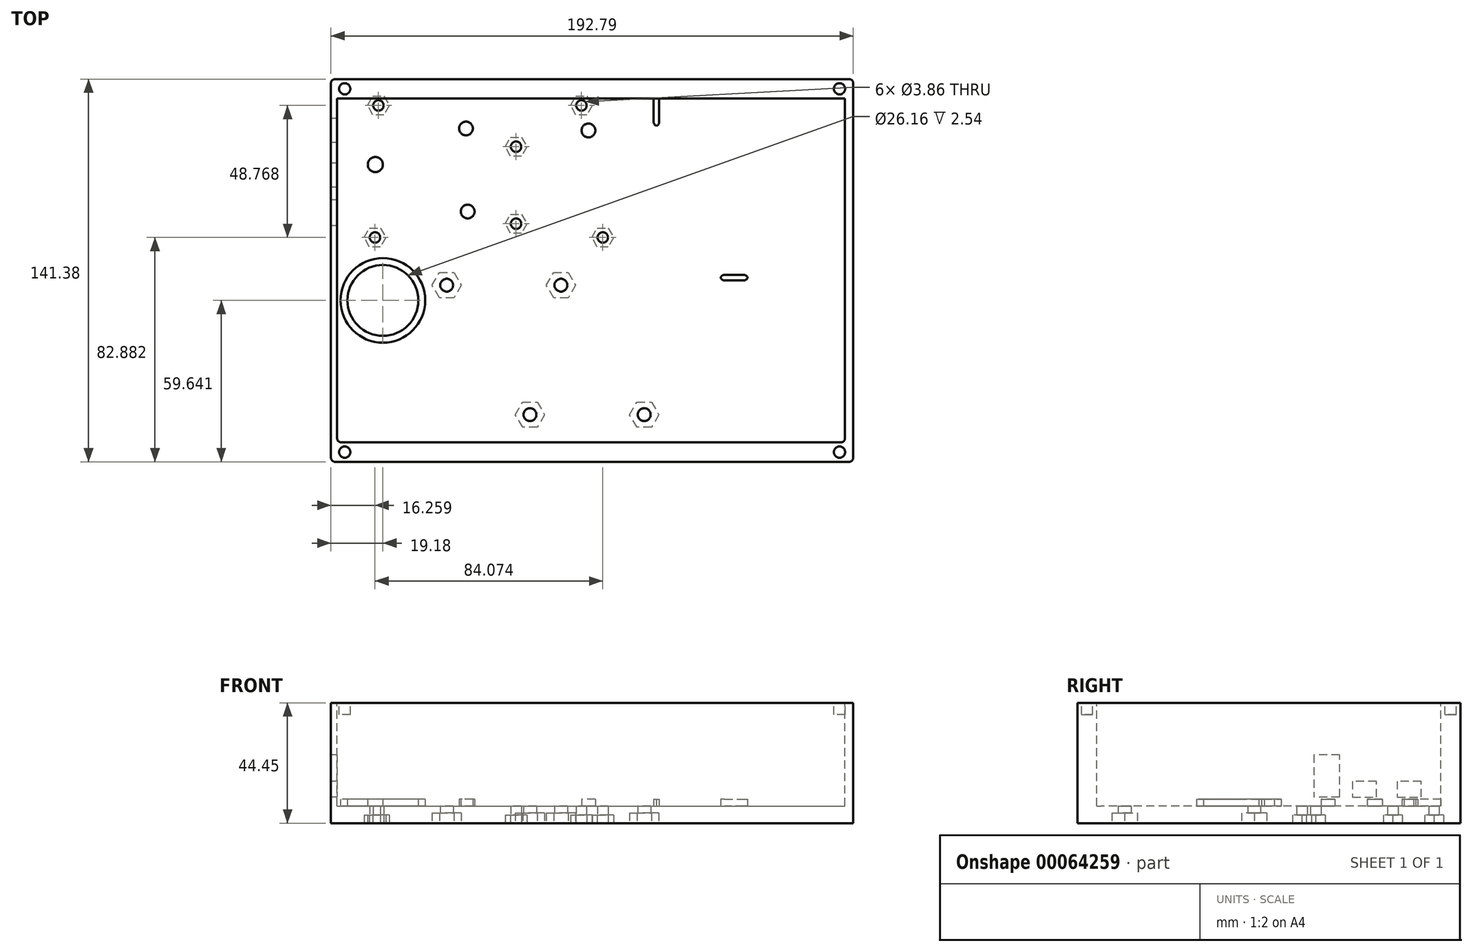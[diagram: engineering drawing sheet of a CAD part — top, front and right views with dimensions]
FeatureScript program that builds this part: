
annotation { "Feature Type Name" : "Feature", "Feature Type Description" : "" }
export const myFeature = defineFeature(function(context is Context, id is Id, definition is map)
    precondition{}
    {
        {
            var Q0;
            Q0=qCreatedBy(makeId("Top.planeOp"),FACE);
            var sketch = newSketch(context, id + "F0", { "sketchPlane" : qUnion([Q0])});
            skLineSegment(sketch, "E0.bottom", {"start": v(-98.88, 40.37) * mm, "end": v(3.23, 40.37) * mm});
            skLineSegment(sketch, "E0.top", {"start": v(-98.88, -13.48) * mm, "end": v(3.23, -13.48) * mm});
            skLineSegment(sketch, "E0.left", {"start": v(-98.88, 40.37) * mm, "end": v(-98.88, -13.48) * mm});
            skLineSegment(sketch, "E0.right", {"start": v(3.23, 40.37) * mm, "end": v(3.23, -13.48) * mm});
            skSolve(sketch);
        }
        {
            var Q0;
            Q0=qCreatedBy(makeId("Top.planeOp"),FACE);
            var sketch = newSketch(context, id + "F1", { "sketchPlane" : qUnion([Q0])});
            skLineSegment(sketch, "E1.bottom", {"start": v(-98.88, 40.37) * mm, "end": v(88.57, 40.37) * mm});
            skLineSegment(sketch, "E1.top", {"start": v(-98.88, -86.63) * mm, "end": v(88.57, -86.63) * mm});
            skLineSegment(sketch, "E1.left", {"start": v(-98.88, 40.37) * mm, "end": v(-98.88, -86.63) * mm});
            skLineSegment(sketch, "E1.right", {"start": v(88.57, 40.37) * mm, "end": v(88.57, -86.63) * mm});
            skSolve(sketch);
        }
        {
            var Q0;
            Q0=qCreatedBy(makeId("Top.planeOp"),FACE);
            var sketch = newSketch(context, id + "F2", { "sketchPlane" : qUnion([Q0])});
            skLineSegment(sketch, "E2", {"start": v(5.77, 40.37) * mm, "end": v(5.77, 30.21) * mm});
            skLineSegment(sketch, "E3", {"start": v(5.77, 30.21) * mm, "end": v(3.23, 30.21) * mm});
            skLineSegment(sketch, "E4", {"start": v(3.23, 30.21) * mm, "end": v(3.23, 40.37) * mm});
            skLineSegment(sketch, "E5", {"start": v(3.23, -3.32) * mm, "end": v(5.77, -3.32) * mm});
            skLineSegment(sketch, "E6", {"start": v(5.77, -3.32) * mm, "end": v(5.77, -16.02) * mm});
            skLineSegment(sketch, "E7", {"start": v(5.77, -16.02) * mm, "end": v(-6.93, -16.02) * mm});
            skLineSegment(sketch, "E8", {"start": v(-6.93, -16.02) * mm, "end": v(-6.93, -13.48) * mm});
            skLineSegment(sketch, "E9", {"start": v(-6.93, -13.48) * mm, "end": v(3.23, -13.48) * mm});
            skLineSegment(sketch, "E10", {"start": v(3.23, -13.48) * mm, "end": v(3.23, -3.32) * mm});
            skLineSegment(sketch, "E11", {"start": v(-6.93, -16.02) * mm, "end": v(-98.88, -16.02) * mm, "construction": true});
            skLineSegment(sketch, "E12", {"start": v(3.23, 40.37) * mm, "end": v(5.77, 40.37) * mm});
            skSolve(sketch);
        }
        {
            var Q0;
            Q0=qCreatedBy(makeId("Top.planeOp"),FACE);
            var sketch = newSketch(context, id + "F3", { "sketchPlane" : qUnion([Q0])});
            skCircle(sketch, "E13", {"center": v(-84.91, -10.94) * mm, "radius": 1.93 * mm});
            skCircle(sketch, "E14", {"center": v(-32.84, -5.86) * mm, "radius": 1.93 * mm});
            skCircle(sketch, "E15", {"center": v(-32.84, 22.6) * mm, "radius": 1.93 * mm});
            skCircle(sketch, "E16", {"center": v(-8.71, 37.83) * mm, "radius": 1.93 * mm});
            skCircle(sketch, "E17", {"center": v(-83.64, 37.83) * mm, "radius": 1.93 * mm});
            skCircle(sketch, "E18", {"center": v(-0.84, -10.94) * mm, "radius": 1.93 * mm});
            skLineSegment(sketch, "E19", {"start": v(-32.84, 40.38) * mm, "end": v(-32.84, -13.48) * mm, "construction": true});
            skLineSegment(sketch, "E20", {"start": v(-32.84, 22.6) * mm, "end": v(3.23, 22.6) * mm, "construction": true});
            skSolve(sketch);
        }
        {
            var Q0;
            Q0=qCreatedBy(makeId("Top.planeOp"),FACE);
            var sketch = newSketch(context, id + "F4", { "sketchPlane" : qUnion([Q0])});
            skCircle(sketch, "E21", {"center": v(-81.99, -34.18) * mm, "radius": 13.08 * mm});
            skCircle(sketch, "E22", {"center": v(-81.99, -34.18) * mm, "radius": 15.62 * mm});
            skSolve(sketch);
        }
        {
            var Q0;
            Q0=qCreatedBy(makeId("Top.planeOp"),FACE);
            var sketch = newSketch(context, id + "F5", { "sketchPlane" : qUnion([Q0])});
            skLineSegment(sketch, "E23.bottom", {"start": v(-101.17, 47.56) * mm, "end": v(91.62, 47.56) * mm});
            skLineSegment(sketch, "E23.top", {"start": v(-101.17, -93.82) * mm, "end": v(91.62, -93.82) * mm});
            skLineSegment(sketch, "E23.left", {"start": v(-101.17, 47.56) * mm, "end": v(-101.17, -93.82) * mm});
            skLineSegment(sketch, "E23.right", {"start": v(91.62, 47.56) * mm, "end": v(91.62, -93.82) * mm});
            skSolve(sketch);
        }
        {
            var Q0;
            Q0=makeQuery(id+"F5.imprint","IMPRINT",FACE,{"disambiguationData":[TD([[makeQuery(id+"F5.imprint","IMPRINT",EDGE,{"derivedFrom":sQuery(id+"F5.wireOp",EDGE,"E23.bottom")}),-1.0]])]});
            var sketch = newSketch(context, id + "F6", { "sketchPlane" : qUnion([Q0])});
            skCircle(sketch, "E24.cCircle", {"center": v(-83.64, 37.83) * mm, "radius": 3.5 * mm, "construction": true});
            skLineSegment(sketch, "E24.0", {"start": v(-79.6, 37.83) * mm, "end": v(-81.62, 34.34) * mm});
            skLineSegment(sketch, "E24.1", {"start": v(-81.62, 34.34) * mm, "end": v(-85.66, 34.34) * mm});
            skLineSegment(sketch, "E24.2", {"start": v(-85.66, 34.34) * mm, "end": v(-87.67, 37.83) * mm});
            skLineSegment(sketch, "E24.3", {"start": v(-87.67, 37.83) * mm, "end": v(-85.66, 41.32) * mm});
            skLineSegment(sketch, "E24.4", {"start": v(-85.66, 41.32) * mm, "end": v(-81.62, 41.32) * mm});
            skLineSegment(sketch, "E24.5", {"start": v(-81.62, 41.32) * mm, "end": v(-79.6, 37.83) * mm});
            skPoint(sketch, "E24.0.midPoint", {"position": v(-80.62, 36.08) * mm});
            skCircle(sketch, "E25.cCircle", {"center": v(-8.71, 37.83) * mm, "radius": 3.5 * mm, "construction": true});
            skLineSegment(sketch, "E25.0", {"start": v(-4.68, 37.83) * mm, "end": v(-6.7, 34.34) * mm});
            skLineSegment(sketch, "E25.1", {"start": v(-6.7, 34.34) * mm, "end": v(-10.73, 34.34) * mm});
            skLineSegment(sketch, "E25.2", {"start": v(-10.73, 34.34) * mm, "end": v(-12.74, 37.83) * mm});
            skLineSegment(sketch, "E25.3", {"start": v(-12.74, 37.83) * mm, "end": v(-10.73, 41.32) * mm});
            skLineSegment(sketch, "E25.4", {"start": v(-10.73, 41.32) * mm, "end": v(-6.7, 41.32) * mm});
            skLineSegment(sketch, "E25.5", {"start": v(-6.7, 41.32) * mm, "end": v(-4.68, 37.83) * mm});
            skPoint(sketch, "E25.0.midPoint", {"position": v(-5.69, 36.08) * mm});
            skCircle(sketch, "E26.cCircle", {"center": v(-32.84, 22.6) * mm, "radius": 3.5 * mm, "construction": true});
            skLineSegment(sketch, "E26.0", {"start": v(-28.8, 22.6) * mm, "end": v(-30.82, 19.1) * mm});
            skLineSegment(sketch, "E26.1", {"start": v(-30.82, 19.1) * mm, "end": v(-34.86, 19.1) * mm});
            skLineSegment(sketch, "E26.2", {"start": v(-34.86, 19.1) * mm, "end": v(-36.87, 22.6) * mm});
            skLineSegment(sketch, "E26.3", {"start": v(-36.87, 22.6) * mm, "end": v(-34.86, 26.08) * mm});
            skLineSegment(sketch, "E26.4", {"start": v(-34.86, 26.08) * mm, "end": v(-30.82, 26.08) * mm});
            skLineSegment(sketch, "E26.5", {"start": v(-30.82, 26.08) * mm, "end": v(-28.8, 22.6) * mm});
            skPoint(sketch, "E26.0.midPoint", {"position": v(-29.82, 20.84) * mm});
            skCircle(sketch, "E27.cCircle", {"center": v(-84.91, -10.94) * mm, "radius": 3.5 * mm, "construction": true});
            skLineSegment(sketch, "E27.0", {"start": v(-80.88, -10.94) * mm, "end": v(-82.9, -14.43) * mm});
            skLineSegment(sketch, "E27.1", {"start": v(-82.9, -14.43) * mm, "end": v(-86.93, -14.43) * mm});
            skLineSegment(sketch, "E27.2", {"start": v(-86.93, -14.43) * mm, "end": v(-88.94, -10.94) * mm});
            skLineSegment(sketch, "E27.3", {"start": v(-88.94, -10.94) * mm, "end": v(-86.93, -7.45) * mm});
            skLineSegment(sketch, "E27.4", {"start": v(-86.93, -7.45) * mm, "end": v(-82.9, -7.45) * mm});
            skLineSegment(sketch, "E27.5", {"start": v(-82.9, -7.45) * mm, "end": v(-80.88, -10.94) * mm});
            skPoint(sketch, "E27.0.midPoint", {"position": v(-81.89, -12.68) * mm});
            skCircle(sketch, "E28.cCircle", {"center": v(-32.84, -5.86) * mm, "radius": 3.5 * mm, "construction": true});
            skLineSegment(sketch, "E28.0", {"start": v(-28.8, -5.86) * mm, "end": v(-30.82, -9.35) * mm});
            skLineSegment(sketch, "E28.1", {"start": v(-30.82, -9.35) * mm, "end": v(-34.86, -9.35) * mm});
            skLineSegment(sketch, "E28.2", {"start": v(-34.86, -9.35) * mm, "end": v(-36.87, -5.86) * mm});
            skLineSegment(sketch, "E28.3", {"start": v(-36.87, -5.86) * mm, "end": v(-34.86, -2.37) * mm});
            skLineSegment(sketch, "E28.4", {"start": v(-34.86, -2.37) * mm, "end": v(-30.82, -2.37) * mm});
            skLineSegment(sketch, "E28.5", {"start": v(-30.82, -2.37) * mm, "end": v(-28.8, -5.86) * mm});
            skPoint(sketch, "E28.0.midPoint", {"position": v(-29.82, -7.6) * mm});
            skCircle(sketch, "E29.cCircle", {"center": v(-0.84, -10.94) * mm, "radius": 3.5 * mm, "construction": true});
            skLineSegment(sketch, "E29.0", {"start": v(3.2, -10.94) * mm, "end": v(1.18, -14.43) * mm});
            skLineSegment(sketch, "E29.1", {"start": v(1.18, -14.43) * mm, "end": v(-2.85, -14.43) * mm});
            skLineSegment(sketch, "E29.2", {"start": v(-2.85, -14.43) * mm, "end": v(-4.87, -10.94) * mm});
            skLineSegment(sketch, "E29.3", {"start": v(-4.87, -10.94) * mm, "end": v(-2.85, -7.45) * mm});
            skLineSegment(sketch, "E29.4", {"start": v(-2.85, -7.45) * mm, "end": v(1.18, -7.45) * mm});
            skLineSegment(sketch, "E29.5", {"start": v(1.18, -7.45) * mm, "end": v(3.2, -10.94) * mm});
            skPoint(sketch, "E29.0.midPoint", {"position": v(2.19, -12.68) * mm});
            skSolve(sketch);
        }
        {
            var Q0;
            Q0 = qSketchRegion(id + "F5", true);
            extrude(context, id + "F7", {"entities" : qUnion([Q0]), "depth" : 44.45 * mm, "offsetDistance" : 25.4 * mm});
        }
        {
            var Q0;
            {var subQ25=sQuery(id+"F5.wireOp",EDGE,"E23.bottom");var subQ26=makeQuery(id+"F7.opExtrude","SWEPT_FACE",FACE,{"disambiguationData":[OSD([subQ25])]});var subQ30=sQuery(id+"F5.wireOp",EDGE,"E23.right");var subQ34=sQuery(id+"F5.wireOp",EDGE,"E23.top");var subQ38=sQuery(id+"F5.wireOp",EDGE,"E23.left");Q0=makeQuery(id+"F15.boolean.opBoolean","SPLIT",FACE,{"disambiguationData":[TD([subQ26])],"derivedFrom":makeQuery(id+"FjWOXJXr2Yc3tZQ_1.boolean.opBoolean","SPLIT",FACE,{"disambiguationData":[TD([subQ26])],"derivedFrom":makeQuery(id+"F7.opExtrude","CAP_FACE",FACE,{"disambiguationData":[OSD([subQ25,subQ34,subQ38,subQ30])],"isStart":false})})});}
            var sketch = newSketch(context, id + "F8", { "sketchPlane" : qUnion([Q0])});
            skLineSegment(sketch, "E30.bottom", {"start": v(-98.88, 40.37) * mm, "end": v(3.23, 40.37) * mm});
            skLineSegment(sketch, "E30.top", {"start": v(-98.88, -13.48) * mm, "end": v(3.23, -13.48) * mm});
            skLineSegment(sketch, "E30.left", {"start": v(-98.88, 40.37) * mm, "end": v(-98.88, -13.48) * mm});
            skLineSegment(sketch, "E30.right", {"start": v(3.23, 40.37) * mm, "end": v(3.23, -13.48) * mm});
            skSolve(sketch);
        }
        {
            var Q0;
            Q0=qCreatedBy(makeId("Top.planeOp"),FACE);
            var sketch = newSketch(context, id + "F9", { "sketchPlane" : qUnion([Q0])});
            skCircle(sketch, "E31.cCircle", {"center": v(-58.43, -28.57) * mm, "radius": 4.67 * mm, "construction": true});
            skLineSegment(sketch, "E31.0", {"start": v(-53.04, -28.57) * mm, "end": v(-55.73, -33.24) * mm});
            skLineSegment(sketch, "E31.1", {"start": v(-55.73, -33.24) * mm, "end": v(-61.13, -33.24) * mm});
            skLineSegment(sketch, "E31.2", {"start": v(-61.13, -33.24) * mm, "end": v(-63.83, -28.57) * mm});
            skLineSegment(sketch, "E31.3", {"start": v(-63.83, -28.57) * mm, "end": v(-61.13, -23.9) * mm});
            skLineSegment(sketch, "E31.4", {"start": v(-61.13, -23.9) * mm, "end": v(-55.73, -23.9) * mm});
            skLineSegment(sketch, "E31.5", {"start": v(-55.73, -23.9) * mm, "end": v(-53.04, -28.57) * mm});
            skPoint(sketch, "E31.0.midPoint", {"position": v(-54.38, -30.9) * mm});
            skCircle(sketch, "E32.cCircle", {"center": v(-27.7, -76.4) * mm, "radius": 4.67 * mm, "construction": true});
            skLineSegment(sketch, "E32.0", {"start": v(-22.3, -76.4) * mm, "end": v(-25, -81.07) * mm});
            skLineSegment(sketch, "E32.1", {"start": v(-25, -81.07) * mm, "end": v(-30.4, -81.07) * mm});
            skLineSegment(sketch, "E32.2", {"start": v(-30.4, -81.07) * mm, "end": v(-33.1, -76.4) * mm});
            skLineSegment(sketch, "E32.3", {"start": v(-33.1, -76.4) * mm, "end": v(-30.4, -71.72) * mm});
            skLineSegment(sketch, "E32.4", {"start": v(-30.4, -71.72) * mm, "end": v(-25, -71.72) * mm});
            skLineSegment(sketch, "E32.5", {"start": v(-25, -71.72) * mm, "end": v(-22.3, -76.4) * mm});
            skPoint(sketch, "E32.0.midPoint", {"position": v(-23.65, -78.73) * mm});
            skCircle(sketch, "E33.cCircle", {"center": v(-16.27, -28.57) * mm, "radius": 4.67 * mm, "construction": true});
            skLineSegment(sketch, "E33.0", {"start": v(-13.57, -23.9) * mm, "end": v(-10.87, -28.57) * mm});
            skLineSegment(sketch, "E33.1", {"start": v(-10.87, -28.57) * mm, "end": v(-13.57, -33.24) * mm});
            skLineSegment(sketch, "E33.2", {"start": v(-13.57, -33.24) * mm, "end": v(-18.97, -33.24) * mm});
            skLineSegment(sketch, "E33.3", {"start": v(-18.97, -33.24) * mm, "end": v(-21.66, -28.57) * mm});
            skLineSegment(sketch, "E33.4", {"start": v(-21.66, -28.57) * mm, "end": v(-18.97, -23.9) * mm});
            skLineSegment(sketch, "E33.5", {"start": v(-18.97, -23.9) * mm, "end": v(-13.57, -23.9) * mm});
            skPoint(sketch, "E33.0.midPoint", {"position": v(-12.22, -26.23) * mm});
            skCircle(sketch, "E34.cCircle", {"center": v(14.47, -76.4) * mm, "radius": 4.67 * mm, "construction": true});
            skLineSegment(sketch, "E34.0", {"start": v(17.16, -71.72) * mm, "end": v(19.86, -76.4) * mm});
            skLineSegment(sketch, "E34.1", {"start": v(19.86, -76.4) * mm, "end": v(17.16, -81.07) * mm});
            skLineSegment(sketch, "E34.2", {"start": v(17.16, -81.07) * mm, "end": v(11.77, -81.07) * mm});
            skLineSegment(sketch, "E34.3", {"start": v(11.77, -81.07) * mm, "end": v(9.07, -76.4) * mm});
            skLineSegment(sketch, "E34.4", {"start": v(9.07, -76.4) * mm, "end": v(11.77, -71.72) * mm});
            skLineSegment(sketch, "E34.5", {"start": v(11.77, -71.72) * mm, "end": v(17.16, -71.72) * mm});
            skPoint(sketch, "E34.0.midPoint", {"position": v(18.51, -74.06) * mm});
            skLineSegment(sketch, "E35", {"start": v(-58.43, -28.57) * mm, "end": v(-27.7, -28.57) * mm, "construction": true});
            skLineSegment(sketch, "E36", {"start": v(-27.7, -28.57) * mm, "end": v(-27.7, -76.4) * mm, "construction": true});
            skLineSegment(sketch, "E37", {"start": v(-16.27, -28.57) * mm, "end": v(14.47, -28.57) * mm});
            skLineSegment(sketch, "E38", {"start": v(14.47, -76.4) * mm, "end": v(14.47, -28.57) * mm});
            skLineSegment(sketch, "E39", {"start": v(-66.37, -20.88) * mm, "end": v(-66.37, -51.5) * mm, "construction": true});
            skSolve(sketch);
        }
        {
            var Q0;
            Q0=qCreatedBy(makeId("Top.planeOp"),FACE);
            var sketch = newSketch(context, id + "F10", { "sketchPlane" : qUnion([Q0])});
            skCircle(sketch, "E40", {"center": v(-58.43, -28.57) * mm, "radius": 2.37 * mm});
            skCircle(sketch, "E41", {"center": v(-27.7, -76.4) * mm, "radius": 2.37 * mm});
            skCircle(sketch, "E42", {"center": v(-16.27, -28.57) * mm, "radius": 2.37 * mm});
            skCircle(sketch, "E43", {"center": v(14.47, -76.4) * mm, "radius": 2.37 * mm});
            skSolve(sketch);
        }
        {
            var Q0;
            Q0=qCreatedBy(makeId("Top.planeOp"),FACE);
            var sketch = newSketch(context, id + "F11", { "sketchPlane" : qUnion([Q0])});
            skCircle(sketch, "E44", {"center": v(-6.14, 28.58) * mm, "radius": 2.54 * mm});
            skCircle(sketch, "E45", {"center": v(-51.31, 29.3) * mm, "radius": 2.54 * mm});
            skCircle(sketch, "E46", {"center": v(-50.7, -1.38) * mm, "radius": 2.54 * mm});
            skCircle(sketch, "E47", {"center": v(-84.77, 15.99) * mm, "radius": 2.8 * mm});
            skSolve(sketch);
        }
        {
            var Q0;
            Q0=makeQuery(id+"F7.opExtrude","CAP_FACE",FACE,{"disambiguationData":[OSD([sQuery(id+"F5.wireOp",EDGE,"E23.bottom"),sQuery(id+"F5.wireOp",EDGE,"E23.top"),sQuery(id+"F5.wireOp",EDGE,"E23.left"),sQuery(id+"F5.wireOp",EDGE,"E23.right")])],"isStart":false});
            var sketch = newSketch(context, id + "F12", { "sketchPlane" : qUnion([Q0])});
            skLineSegment(sketch, "E48.bottom", {"start": v(-98.88, 40.37) * mm, "end": v(88.57, 40.37) * mm});
            skLineSegment(sketch, "E48.top", {"start": v(-98.88, -86.63) * mm, "end": v(88.57, -86.63) * mm});
            skLineSegment(sketch, "E48.left", {"start": v(-98.88, 40.37) * mm, "end": v(-98.88, -86.63) * mm});
            skLineSegment(sketch, "E48.right", {"start": v(88.57, 40.37) * mm, "end": v(88.57, -86.63) * mm});
            skSolve(sketch);
        }
        {
            var Q0;
            Q0=qCreatedBy(makeId("Top.planeOp"),FACE);
            var sketch = newSketch(context, id + "F13", { "sketchPlane" : qUnion([Q0])});
            skLineSegment(sketch, "E49", {"start": v(17.96, 30.21) * mm, "end": v(20, 30.21) * mm});
            skLineSegment(sketch, "E50", {"start": v(17.96, 40.37) * mm, "end": v(17.96, 30.21) * mm});
            skLineSegment(sketch, "E51", {"start": v(52.73, -26.81) * mm, "end": v(52.73, -24.78) * mm});
            skLineSegment(sketch, "E52", {"start": v(52.73, -24.78) * mm, "end": v(42.57, -24.78) * mm});
            skLineSegment(sketch, "E53", {"start": v(20, 40.37) * mm, "end": v(20, 30.21) * mm});
            skLineSegment(sketch, "E54", {"start": v(17.96, 40.37) * mm, "end": v(20, 40.37) * mm});
            skLineSegment(sketch, "E55", {"start": v(42.57, -24.78) * mm, "end": v(42.57, -26.81) * mm});
            skLineSegment(sketch, "E56", {"start": v(42.57, -26.81) * mm, "end": v(52.73, -26.81) * mm});
            skLineSegment(sketch, "E57", {"start": v(20, 40.37) * mm, "end": v(20, -85.45) * mm});
            skSolve(sketch);
        }
        {
            var Q0;
            Q0 = qSketchRegion(id + "F12", true);
            extrude(context, id + "F14", {"entities" : qUnion([Q0]), "operationType" : NewBodyOperationType.REMOVE, "oppositeDirection" : true, "depth" : 38.1 * mm, "offsetDistance" : 25.4 * mm});
        }
        {
            var Q0;
            Q0 = qSketchRegion(id + "F4", true);
            var Q1;
            Q1 = qSketchRegion(id + "F13", true);
            extrude(context, id + "F15", {"entities" : qUnion([Q0, Q1]), "operationType" : NewBodyOperationType.ADD, "depth" : 8.9 * mm, "offsetDistance" : 25.4 * mm});
        }
        {
            var Q0;
            Q0 = qSketchRegion(id + "F6", true);
            extrude(context, id + "F16", {"entities" : qUnion([Q0]), "operationType" : NewBodyOperationType.REMOVE, "depth" : 3 * mm, "offsetDistance" : 25.4 * mm});
        }
        {
            var Q0;
            Q0 = qSketchRegion(id + "F9", true);
            extrude(context, id + "F17", {"entities" : qUnion([Q0]), "operationType" : NewBodyOperationType.REMOVE, "depth" : 3.8 * mm, "offsetDistance" : 25.4 * mm});
        }
        {
            var Q0;
            Q0 = qSketchRegion(id + "F10", true);
            extrude(context, id + "F18", {"entities" : qUnion([Q0]), "operationType" : NewBodyOperationType.REMOVE, "depth" : 25.4 * mm, "offsetDistance" : 25.4 * mm});
        }
        {
            var Q0;
            Q0 = qSketchRegion(id + "F3", true);
            extrude(context, id + "F19", {"entities" : qUnion([Q0]), "operationType" : NewBodyOperationType.REMOVE, "depth" : 25.4 * mm, "offsetDistance" : 25.4 * mm});
        }
        {
            var Q0;
            Q0 = qSketchRegion(id + "F11", true);
            extrude(context, id + "F20", {"entities" : qUnion([Q0]), "operationType" : NewBodyOperationType.ADD, "depth" : 8.9 * mm, "offsetDistance" : 25.4 * mm});
        }
        {
            var Q0;
            Q0=makeQuery(id+"F7.opExtrude","SWEPT_FACE",FACE,{"disambiguationData":[OSD([sQuery(id+"F5.wireOp",EDGE,"E23.left")])]});
            var sketch = newSketch(context, id + "F21", { "sketchPlane" : qUnion([Q0])});
            skLineSegment(sketch, "E58", {"start": v(-47.56, 6.35) * mm, "end": v(93.82, 6.35) * mm, "construction": true});
            skLineSegment(sketch, "E59", {"start": v(-43.75, 44.45) * mm, "end": v(-43.75, 0) * mm, "construction": true});
            skLineSegment(sketch, "E60", {"start": v(-47.56, 9.65) * mm, "end": v(93.82, 9.65) * mm, "construction": true});
            skLineSegment(sketch, "E61", {"start": v(-7.68, 15.5) * mm, "end": v(-7.68, 9.65) * mm});
            skLineSegment(sketch, "E62", {"start": v(-7.68, 9.65) * mm, "end": v(-16.57, 9.65) * mm});
            skLineSegment(sketch, "E63", {"start": v(-16.57, 9.65) * mm, "end": v(-16.57, 15.5) * mm});
            skLineSegment(sketch, "E64", {"start": v(10.1, 15.5) * mm, "end": v(10.1, 9.65) * mm, "construction": true});
            skLineSegment(sketch, "E65", {"start": v(-24.2, 15.5) * mm, "end": v(-24.2, 9.65) * mm});
            skLineSegment(sketch, "E66", {"start": v(-24.2, 9.65) * mm, "end": v(-33.08, 9.65) * mm});
            skLineSegment(sketch, "E67", {"start": v(-33.08, 9.65) * mm, "end": v(-33.08, 15.5) * mm});
            skLineSegment(sketch, "E68", {"start": v(-33.08, 15.5) * mm, "end": v(-24.2, 15.5) * mm});
            skLineSegment(sketch, "E69", {"start": v(-16.57, 15.5) * mm, "end": v(-7.68, 15.5) * mm});
            skLineSegment(sketch, "E70", {"start": v(10.1, 15.5) * mm, "end": v(-47.56, 15.5) * mm, "construction": true});
            skLineSegment(sketch, "E71", {"start": v(6.54, 25.27) * mm, "end": v(6.54, 9.65) * mm});
            skLineSegment(sketch, "E72", {"start": v(-2.98, 9.65) * mm, "end": v(6.54, 9.65) * mm});
            skLineSegment(sketch, "E73", {"start": v(-2.98, 9.65) * mm, "end": v(-2.98, 25.27) * mm});
            skLineSegment(sketch, "E74", {"start": v(-2.98, 25.27) * mm, "end": v(6.54, 25.27) * mm});
            skSolve(sketch);
        }
        {
            var Q0;
            Q0 = qSketchRegion(id + "F21", true);
            extrude(context, id + "F22", {"entities" : qUnion([Q0]), "operationType" : NewBodyOperationType.REMOVE, "oppositeDirection" : true, "depth" : 25.4 * mm, "offsetDistance" : 25.4 * mm});
        }
        {
            var Q0;
            Q0=makeQuery(id+"F12.imprint","IMPRINT",FACE,{"disambiguationData":[TD([[makeQuery(id+"F12.imprint","IMPRINT",EDGE,{"derivedFrom":sQuery(id+"F12.wireOp",EDGE,"E48.bottom")}),1.0]])]});
            var sketch = newSketch(context, id + "F23", { "sketchPlane" : qUnion([Q0])});
            skCircle(sketch, "E75", {"center": v(-96.09, -90.22) * mm, "radius": 2.08 * mm});
            skCircle(sketch, "E76", {"center": v(86.54, -90.22) * mm, "radius": 2.08 * mm});
            skCircle(sketch, "E77", {"center": v(86.54, 43.96) * mm, "radius": 2.08 * mm});
            skCircle(sketch, "E78", {"center": v(-96.09, 43.96) * mm, "radius": 2.08 * mm});
            skSolve(sketch);
        }
        {
            var Q0;
            Q0 = qSketchRegion(id + "F23", true);
            extrude(context, id + "F24", {"entities" : qUnion([Q0]), "operationType" : NewBodyOperationType.REMOVE, "oppositeDirection" : true, "depth" : 4.32 * mm, "offsetDistance" : 25.4 * mm});
        }
        {
            var Q0;
            Q0=makeQuery(id+"F7.opExtrude","SWEPT_EDGE",EDGE,{"disambiguationData":[OSD([sQuery(id+"F5.wireOp",EDGE,"E23.bottom"),sQuery(id+"F5.wireOp",EDGE,"E23.left")])]});
            var Q1;
            Q1=makeQuery(id+"F7.opExtrude","SWEPT_EDGE",EDGE,{"disambiguationData":[OSD([sQuery(id+"F5.wireOp",EDGE,"E23.top"),sQuery(id+"F5.wireOp",EDGE,"E23.left")])]});
            var Q2;
            Q2=makeQuery(id+"F7.opExtrude","SWEPT_EDGE",EDGE,{"disambiguationData":[OSD([sQuery(id+"F5.wireOp",EDGE,"E23.top"),sQuery(id+"F5.wireOp",EDGE,"E23.right")])]});
            var Q3;
            Q3=makeQuery(id+"F7.opExtrude","SWEPT_EDGE",EDGE,{"disambiguationData":[OSD([sQuery(id+"F5.wireOp",EDGE,"E23.bottom"),sQuery(id+"F5.wireOp",EDGE,"E23.right")])]});
            var Q4;
            Q4=makeQuery(id+"F15.opExtrude","SWEPT_EDGE",EDGE,{"disambiguationData":[OSD([sQuery(id+"F13.wireOp",EDGE,"E49"),sQuery(id+"F13.wireOp",EDGE,"E50")])]});
            var Q5;
            Q5=makeQuery(id+"F15.opExtrude","SWEPT_EDGE",EDGE,{"disambiguationData":[OSD([sQuery(id+"F13.wireOp",EDGE,"E55"),sQuery(id+"F13.wireOp",EDGE,"E56")])]});
            var Q6;
            Q6=makeQuery(id+"F15.opExtrude","SWEPT_EDGE",EDGE,{"disambiguationData":[OSD([sQuery(id+"F13.wireOp",EDGE,"E52"),sQuery(id+"F13.wireOp",EDGE,"E55")])]});
            var Q7;
            Q7=makeQuery(id+"F15.opExtrude","SWEPT_EDGE",EDGE,{"disambiguationData":[OSD([sQuery(id+"F13.wireOp",EDGE,"E49"),sQuery(id+"F13.wireOp",EDGE,"E57")])]});
            var Q8;
            Q8=makeQuery(id+"F15.opExtrude","SWEPT_EDGE",EDGE,{"disambiguationData":[OSD([sQuery(id+"F13.wireOp",EDGE,"E51"),sQuery(id+"F13.wireOp",EDGE,"E56")])]});
            var Q9;
            Q9=makeQuery(id+"F15.opExtrude","SWEPT_EDGE",EDGE,{"disambiguationData":[OSD([sQuery(id+"F13.wireOp",EDGE,"E51"),sQuery(id+"F13.wireOp",EDGE,"E52")])]});
            var Q10;
            Q10=makeQuery(id+"F14.boolean.opBoolean","COPY",EDGE,{"derivedFrom":makeQuery(id+"F14.opExtrude","SWEPT_EDGE",EDGE,{"disambiguationData":[OSD([sQuery(id+"F12.wireOp",EDGE,"E48.top"),sQuery(id+"F12.wireOp",EDGE,"E48.left")])]})});
            var Q11;
            Q11=makeQuery(id+"F14.boolean.opBoolean","COPY",EDGE,{"derivedFrom":makeQuery(id+"F14.opExtrude","SWEPT_EDGE",EDGE,{"disambiguationData":[OSD([sQuery(id+"F12.wireOp",EDGE,"E48.top"),sQuery(id+"F12.wireOp",EDGE,"E48.right")])]})});
            fillet(context, id + "F25", {"entities" : qUnion([Q0, Q1, Q2, Q3, Q4, Q5, Q6, Q7, Q8, Q9, Q10, Q11]), "radius" : 1.52 * mm, "tangentPropagation" : true, "allowEdgeOverflow" : false});
        }
    });
